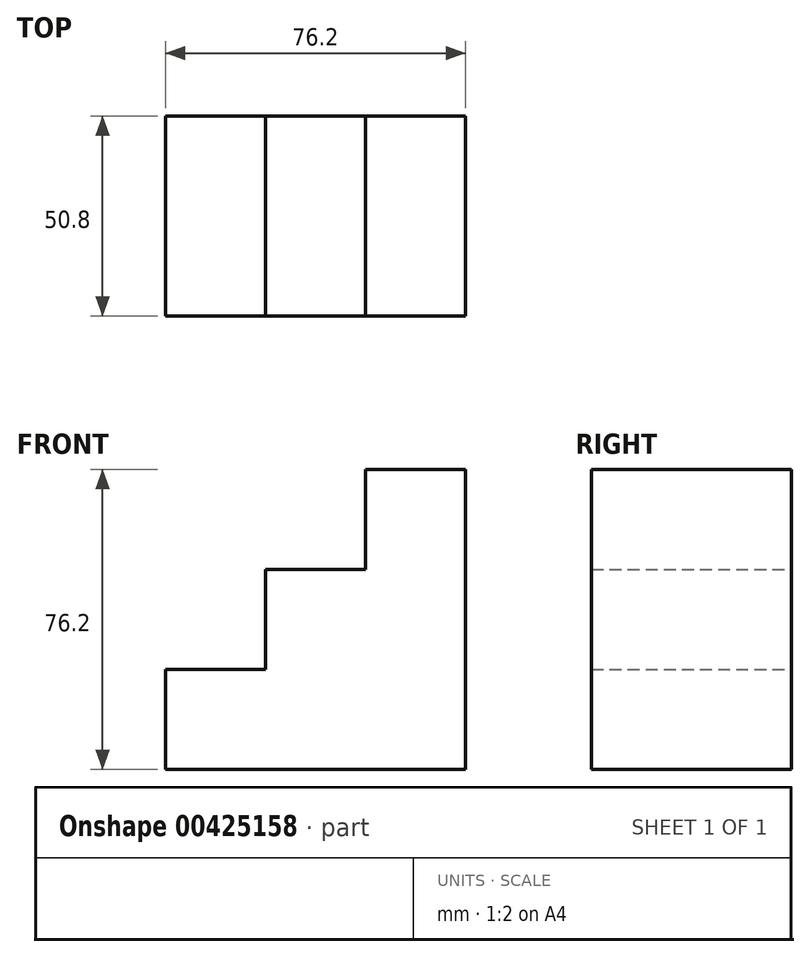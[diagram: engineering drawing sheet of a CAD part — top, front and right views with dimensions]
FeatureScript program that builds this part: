
annotation { "Feature Type Name" : "Feature", "Feature Type Description" : "" }
export const myFeature = defineFeature(function(context is Context, id is Id, definition is map)
    precondition{}
    {
        {
            var Q0;
            Q0=qCreatedBy(makeId("Front.planeOp"),FACE);
            var sketch = newSketch(context, id + "F0", { "sketchPlane" : qUnion([Q0])});
            skPoint(sketch, "E0.start.orphan", {"position": v(-35.17, 0) * mm});
            skLineSegment(sketch, "E1", {"start": v(-35.17, 0) * mm, "end": v(41.03, 0) * mm});
            skLineSegment(sketch, "E2", {"start": v(41.03, 0) * mm, "end": v(41.03, 76.2) * mm});
            skLineSegment(sketch, "E3", {"start": v(41.03, 76.2) * mm, "end": v(15.63, 76.2) * mm});
            skLineSegment(sketch, "E4", {"start": v(15.63, 76.2) * mm, "end": v(15.63, 50.8) * mm});
            skLineSegment(sketch, "E5", {"start": v(15.63, 50.8) * mm, "end": v(-9.77, 50.8) * mm});
            skLineSegment(sketch, "E6", {"start": v(-9.77, 50.8) * mm, "end": v(-9.77, 25.4) * mm});
            skLineSegment(sketch, "E7", {"start": v(-9.77, 25.4) * mm, "end": v(-35.17, 25.4) * mm});
            skLineSegment(sketch, "E8", {"start": v(-35.17, 25.4) * mm, "end": v(-35.17, 0) * mm});
            skSolve(sketch);
        }
        {
            var Q0;
            Q0 = qSketchRegion(id + "F0", true);
            extrude(context, id + "F1", {"entities" : qUnion([Q0]), "depth" : 50.8 * mm});
        }
    });
